# Revit family: Firestop-Wrap_Strip-STI-Series_SS_WBLU_Sealant_1_to_4_floor
name_source: partatom
category: Specialty Equipment
units: mm (PartAtom-declared; Revit-internal decimal feet)

## family parameters
Always vertical = Yes
Classification Number = 23.20.50.14.11
Cut with Voids When Loaded = No
Enable Cutting in Views = No
Host = Floor
Maintain Annotation Orientation = No
Part Type = Normal
Room Calculation Point = No
Round Connector Dimension = Use Diameter
Shared = No

## types (6) — shared parameters
Assembly Code = D4030900
Default Elevation = 0' - 0"
Description = Blue Wrap Strip (2" X 3/16" X 12')
Fire Rating = Up to 4 Hr
Firestop_STI_Intumescent-Blue = STI Molded Intrumescent Insert blu
Galvanized_STI_Steel-Collar = Rap
Green Building/LEED® Information = http://sti.fmpdata.net
Guide Specification = http://www.stifirestop.com
Locate Distributor = http://www.stifirestop.com
MSDS = http://files.systems.stifirestop.com
Manufacturer = Specified Technologies Inc.
Manufacturer Fax No. = 908.526.9623
Model = SSWBLU
Product Documentation Link = http://files.systems.stifirestop.com
Product Page URL = http://www.stifirestop.com
Tested Systems = http://sti.fmpdata.net
URL = http://www.stifirestop.com

## per-type parameters (varying)
| type | Color | ID of Collar | Material | Mounting Tab ID | Mounting Tabs Large Width | Mounting Tabs Small Width | Pipe OD | Screw Hole Width | Stack height |
| 01.5 Pipe |  | 0' - 2 9/32" |  | 0' - 1 3/32" | 0' - 0 3/4" | 0' - 0 9/16" | 0' - 1 29/32" | 0' - 0 5/16" | 0' - 2" |
| 02 Pipe |  | 0' - 2 3/4" |  | 0' - 1 5/16" | 0' - 0 3/4" | 0' - 0 9/16" | 0' - 2 3/8" | 0' - 0 5/16" | 0' - 2" |
| 02.5 Pipe |  | 0' - 3 5/8" |  | 0' - 1 3/4" | 0' - 0 3/4" | 0' - 0 9/16" | 0' - 2 7/8" | 0' - 0 5/16" | 0' - 2" |
| 03 Pipe |  | 0' - 4 1/4" |  | 0' - 2 1/16" | 0' - 1" | 0' - 0 1/2" | 0' - 3 1/2" | 0' - 0 3/8" | 0' - 1 1/2" |
| 03.5 Pipe |  | 0' - 5 1/8" |  | 0' - 2 1/2" | 0' - 1" | 0' - 0 1/2" | 0' - 4" | 0' - 0 3/8" | 0' - 2" |
| 04 Pipe | BLUE | 0' - 5 5/8" | Flexible intumescent strip faced with plastic | 0' - 2 3/4" | 0' - 1" | 0' - 0 1/2" | 0' - 4 1/2" | 0' - 0 3/8" | 0' - 2" |

## geometry (parser evidence)
native form markers: Blend x8, Sweep x3
no freeform markers — native parametric forms only
